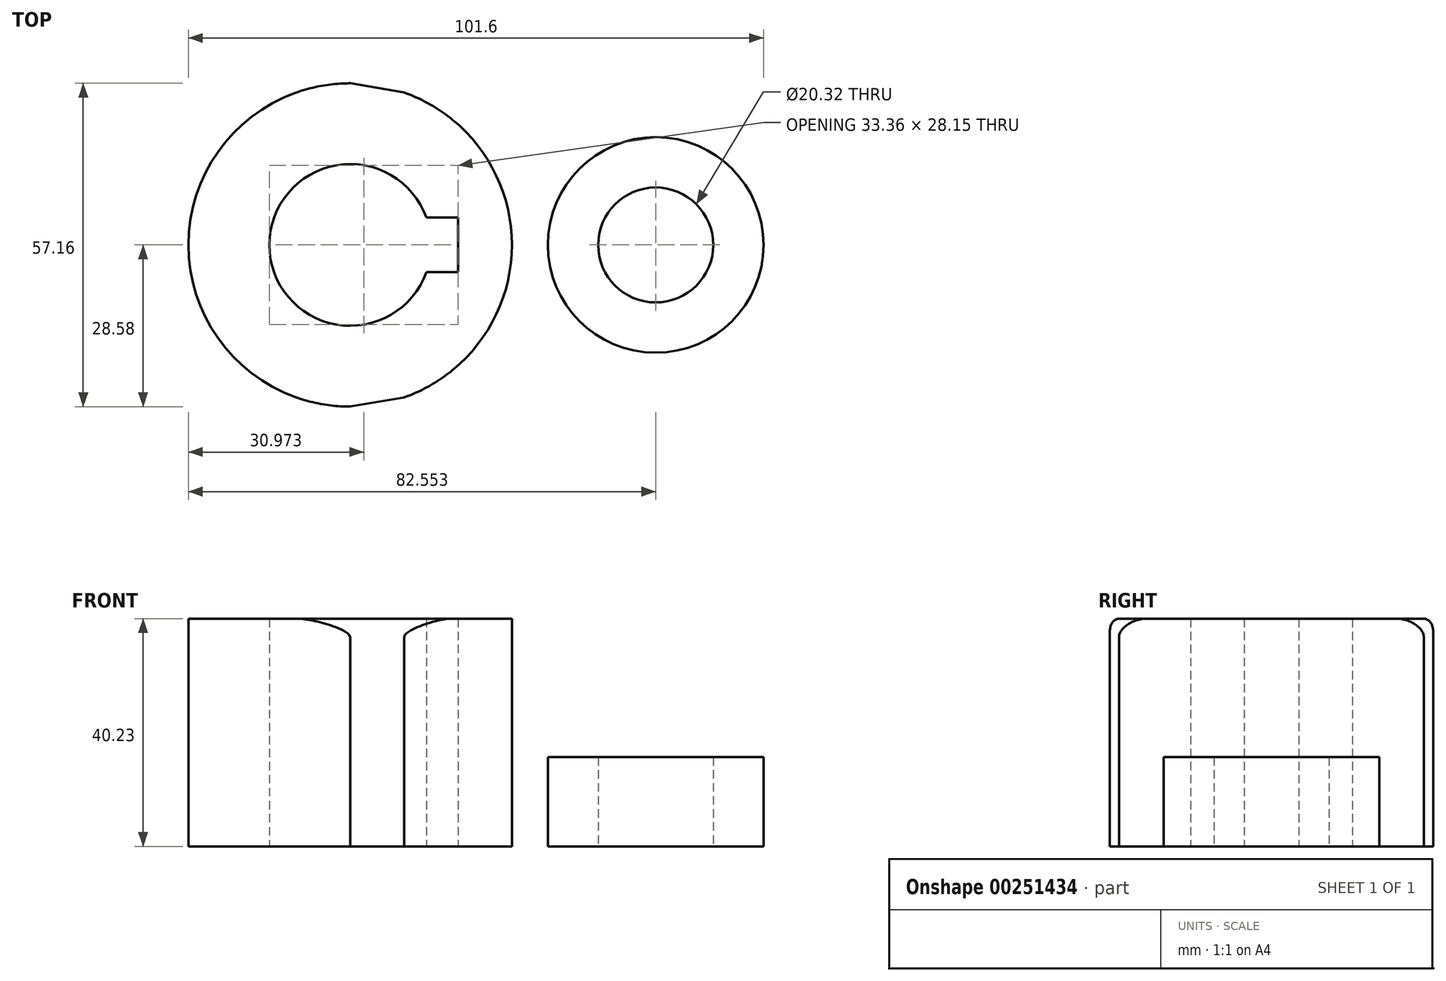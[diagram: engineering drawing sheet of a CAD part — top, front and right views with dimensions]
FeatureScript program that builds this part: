
annotation { "Feature Type Name" : "Feature", "Feature Type Description" : "" }
export const myFeature = defineFeature(function(context is Context, id is Id, definition is map)
    precondition{}
    {
        {
            var Q0;
            Q0=qCreatedBy(makeId("Top.planeOp"),FACE);
            var sketch = newSketch(context, id + "F0", { "sketchPlane" : qUnion([Q0])});
            skArc(sketch, "E0", {"start": v(-15.76, 4.83) * mm, "mid": v(-43.5, 0) * mm, "end": v(-15.76, -4.83) * mm});
            skCircle(sketch, "E1", {"center": v(24.76, 0) * mm, "radius": 10.16 * mm});
            skCircle(sketch, "E2", {"center": v(-29.21, 0) * mm, "radius": 28.58 * mm});
            skCircle(sketch, "E3", {"center": v(24.76, 0) * mm, "radius": 19.05 * mm});
            skPoint(sketch, "E4.visualSharp", {"position": v(33.04, -28.58) * mm});
            skLineSegment(sketch, "E5", {"start": v(-29.21, -28.58) * mm, "end": v(27.98, -18.78) * mm});
            skLineSegment(sketch, "E6", {"start": v(-29.21, 28.58) * mm, "end": v(27.98, 18.78) * mm});
            skLineSegment(sketch, "E7.right", {"start": v(-10.13, -4.83) * mm, "end": v(-10.13, 4.83) * mm});
            skLineSegment(sketch, "E8.trimOffspring", {"start": v(-15.76, 4.83) * mm, "end": v(-10.13, 4.83) * mm});
            skLineSegment(sketch, "E9.trimOffspring", {"start": v(-15.76, -4.83) * mm, "end": v(-10.13, -4.83) * mm});
            skSolve(sketch);
        }
        {
            var Q0;
            Q0=makeQuery(id+"F0.imprint","IMPRINT",FACE,{"disambiguationData":[TD([[makeQuery(id+"F0.imprint","IMPRINT",EDGE,{"derivedFrom":sQuery(id+"F0.wireOp",EDGE,"E0")}),-1.0]])]});
            extrude(context, id + "F1", {"entities" : qUnion([Q0]), "depth" : 40.23 * mm});
        }
        {
            var Q0;
            {var subQ0=sQuery(id+"F0.wireOp",EDGE,"E6");var subQ1=sQuery(id+"F0.wireOp",EDGE,"E2");var subQ2=makeQuery(id+"F0.imprint","INTERSECT",VERTEX,{"disambiguationData":[OD(1.0)],"derivedFrom":[subQ1,subQ0]});Q0=makeQuery(id+"F0.imprint","IMPRINT",FACE,{"disambiguationData":[TD([[makeQuery(id+"F0.imprint","IMPRINT",EDGE,{"disambiguationData":[TD([[subQ2,1.0]])],"derivedFrom":subQ1}),-1.0]])]});}
            var Q1;
            Q1=makeQuery(id+"F0.imprint","IMPRINT",FACE,{"disambiguationData":[TD([[makeQuery(id+"F0.imprint","IMPRINT",EDGE,{"derivedFrom":sQuery(id+"F0.wireOp",EDGE,"E1")}),-1.0]])]});
            extrude(context, id + "F2", {"entities" : qUnion([Q0, Q1]), "operationType" : NewBodyOperationType.ADD, "depth" : 15.77 * mm});
        }
        {
            var Q0;
            {var subQ0=sQuery(id+"F0.wireOp",EDGE,"E2");Q0=makeQuery(id+"F1.opExtrude","CAP_EDGE",EDGE,{"disambiguationData":[OSD([subQ0]),TDD([makeQuery(id+"F0.imprint","IMPRINT",EDGE,{"disambiguationData":[TD([[makeQuery(id+"F0.imprint","INTERSECT",VERTEX,{"disambiguationData":[OD(0.0)],"derivedFrom":[subQ0,sQuery(id+"F0.wireOp",EDGE,"E5")]}),1.0]])],"derivedFrom":subQ0})])],"isStart":false});}
            var Q1;
            Q1=makeQuery(id+"F1.opExtrude","CAP_EDGE",EDGE,{"disambiguationData":[OSD([sQuery(id+"F0.wireOp",EDGE,"E5")])],"isStart":false});
            var Q2;
            {var subQ0=sQuery(id+"F0.wireOp",EDGE,"E2");Q2=makeQuery(id+"F1.opExtrude","CAP_EDGE",EDGE,{"disambiguationData":[OSD([subQ0]),TDD([makeQuery(id+"F0.imprint","IMPRINT",EDGE,{"disambiguationData":[TD([[makeQuery(id+"F0.imprint","INTERSECT",VERTEX,{"disambiguationData":[OD(1.0)],"derivedFrom":[subQ0,sQuery(id+"F0.wireOp",EDGE,"E6")]}),1.0]])],"derivedFrom":subQ0})])],"isStart":false});}
            var Q3;
            Q3=makeQuery(id+"F1.opExtrude","CAP_EDGE",EDGE,{"disambiguationData":[OSD([sQuery(id+"F0.wireOp",EDGE,"E6")])],"isStart":false});
            fillet(context, id + "F3", {"entities" : qUnion([Q0, Q1, Q2, Q3]), "radius" : 3.3 * mm, "tangentPropagation" : true, "allowEdgeOverflow" : false});
        }
    });
